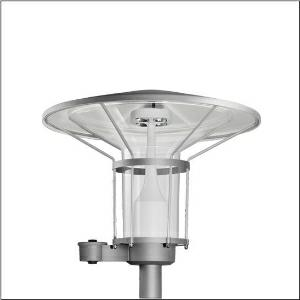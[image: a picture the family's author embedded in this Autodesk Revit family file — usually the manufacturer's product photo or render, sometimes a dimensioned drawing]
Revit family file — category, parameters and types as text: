
# Revit family: laterne_classic_iq___st1_2a_5xa5245ev14h000022_e0c1
name_source: partatom
category: Lighting Fixtures
units: mm (PartAtom-declared; Revit-internal decimal feet)

## family parameters
Cut with Voids When Loaded = No
Host = Face
Light Source = No
Part Type = Normal
Room Calculation Point = No
Round Connector Dimension = Use Diameter
Shared = No

## types (1)
- --- (1 x LED, 1370 lm, 10.7 W, 3000K)
    Apparent Load = 11 VA
    CIE Flux Codes = 21 60 93 97 100
    Color Rendering = 70
    Color Temperature = 3000K
    Default Elevation = 1800 mm
    Description = Lantern Classic iQ, mast luminaire, Module 540 iQ-SR, primary light control with 3 zone facetted reflector, of plastic, silver coated, highly specular, structured, primary optical cover: cover, of PMMA, transparent, light distribution: ST1.2a, light emission: direct distribution, primary light characteristic: asymmetric, installation type: post-top, LED, High Power LED, rated luminous flux: 1.370lm, luminous efficacy: 128lm/W, light colour: 730, colour temperature: 3000K, control gear: iQ-Street Remote, D4i with power reduction, control: optimised constant luminous flux control (CLO 2.0), Desk-Remote (wireless, voltage-free reading and setting of iQ features in the workshop via application-optimized NFC function/RFID function), Light-Fading, Smart-Wire, Night-Set, Lumen-Switch, Temp-Guard, Auto-Match, Street-Remote, pre-setting: logarithmic dimming characteristic, with terminal, 6-pole, max. 2.5mm², mains connection: 230..240V, AC, 50/60Hz, connection cable pre-assembled, cable length: 5,5m, wiring characteristics: H07RN-F, start of lifetime: 11W, end of service life: 11W, reduction: 6W, luminaire housing, upper part, of glass-fibre reinforced polyester, coated, Siteco® metallic grey (DB 702S), diameter: 750mm, height: 596mm, spigot size: d x l = 76 x 70mm (post-top) | with reducer (optional accessory) 60 x 70mm, mounting height: 3..5m, post-top mast mounting element, of diecast aluminium, coated, Siteco® metallic grey (DB 702S), Module 540 iQ-SR, traffic white (RAL 9016), equipment: standard, Smart Interface above, protection rating (complete): IP65, insulation class (complete): insulation class II (safety insulation), certification: CE, ENEC, VDE, packaging unit: 1 piece

Light Distribution: ST1.2a
    Height = 596 mm
    Lamp = 1 x LED
    Lamp Light Flux = 1370 lm
    Lamp Power = 10.7 W
    Lamp count = 1
    Length = 750 mm
    Luminous efficacy = 128 lm/W
    Manufacturer = Siteco
    ModVariant = No
    Model = 5XA5245EV14H000022
    Number of Poles = 1
    OnlyDefault = Yes
    Power Factor = 1
    Product Name = Laterne Classic iQ | ST1.2a
    Product group = mast luminaire | pylon top
    ProductGroupID = 6100
    Protection Class = Protection class II
    Protection Degree = IP 65
    RLX_Detail_Level = 1
    RLX_Emergency_Light_Flux = 0 lm
    RLX_Emergency_Type = 0
    RLX_Emergency_Type_DB = No
    RlxData = <blob elided: 63889 chars, md5=844f85d4>
    Socket = socket
    Standby Power = 0 W
    System Light Flux = 1370 lm
    System Power = 11 W
    Type Comments = factory setting: luminous flux: 100 % | dim-lin: 254 | 419 mA
    Type Image = l_1006522.jpg
    URL = http://relux.com
    VarID = @adj_108121
    Voltage = 0 V
    Weight = 0.00 kg
    Width = 0 mm  [stored 0 ft]

note: [stored X ft] marks values corroborated as IEEE doubles in the binary element streams (Revit-internal decimal feet)

## geometry (parser evidence)
native form markers: Blend x4, Sweep x10
no freeform markers — native parametric forms only
